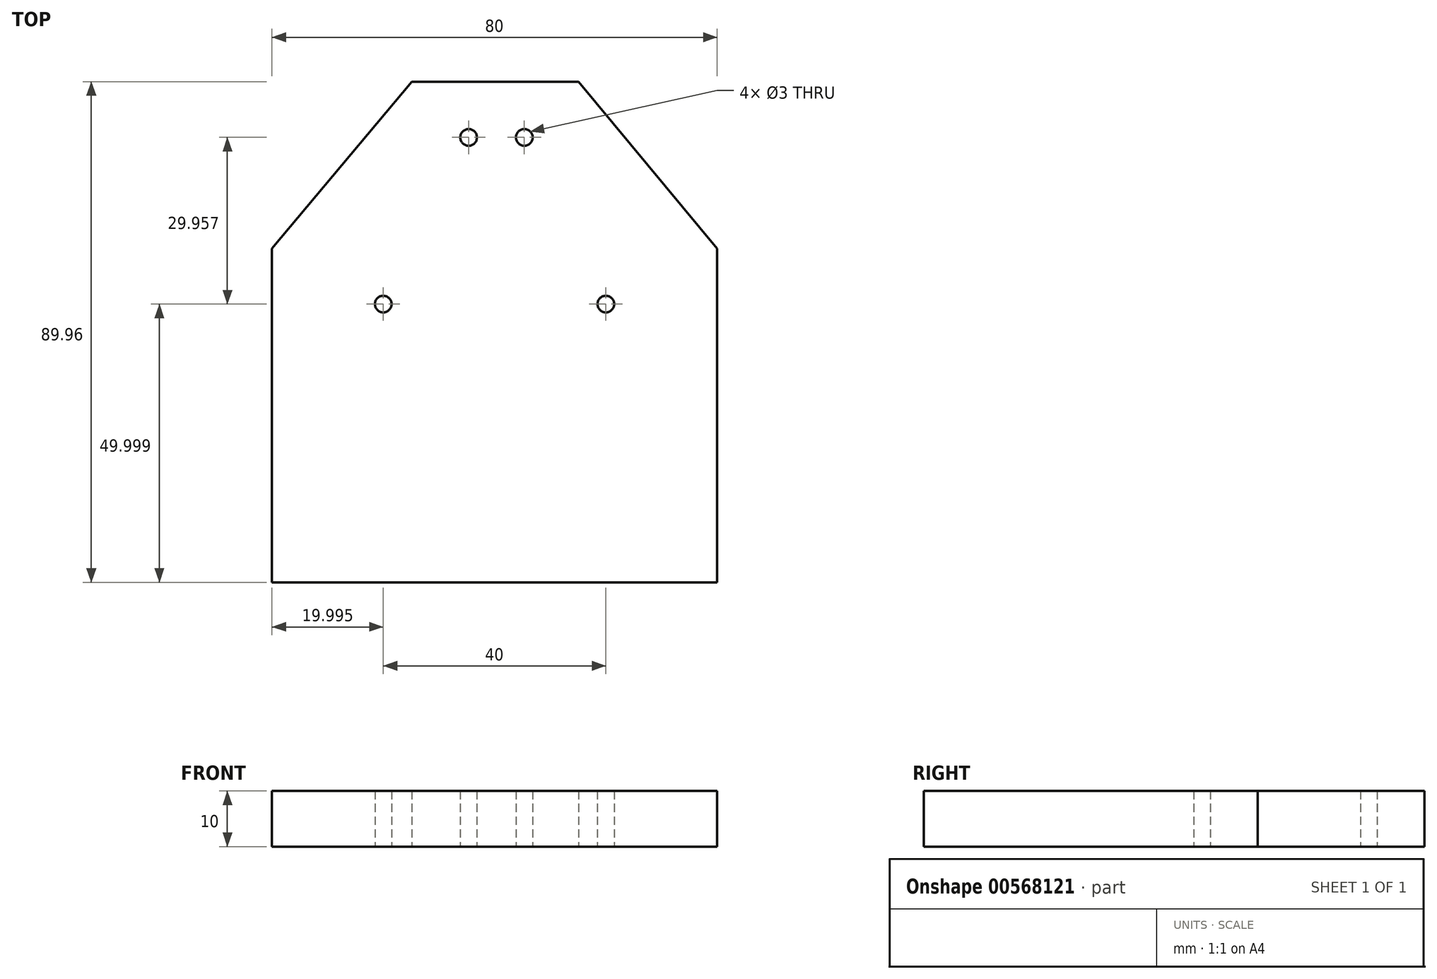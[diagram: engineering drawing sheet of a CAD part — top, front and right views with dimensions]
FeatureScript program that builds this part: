
annotation { "Feature Type Name" : "Feature", "Feature Type Description" : "" }
export const myFeature = defineFeature(function(context is Context, id is Id, definition is map)
    precondition{}
    {
        {
            var Q0;
            Q0=qCreatedBy(makeId("Top.planeOp"),FACE);
            var sketch = newSketch(context, id + "F0", { "sketchPlane" : qUnion([Q0])});
            skLineSegment(sketch, "E0", {"start": v(-40.34, 6.79) * mm, "end": v(39.66, 6.79) * mm});
            skLineSegment(sketch, "E1", {"start": v(39.66, 6.79) * mm, "end": v(39.66, 66.79) * mm});
            skLineSegment(sketch, "E2", {"start": v(-40.34, 6.79) * mm, "end": v(-40.34, 66.79) * mm});
            skLineSegment(sketch, "E3", {"start": v(-15.22, 96.75) * mm, "end": v(14.78, 96.75) * mm});
            skLineSegment(sketch, "E4", {"start": v(0, 66.79) * mm, "end": v(0, 96.79) * mm, "construction": true});
            skLineSegment(sketch, "E5", {"start": v(-15.22, 96.75) * mm, "end": v(-40.34, 66.79) * mm});
            skLineSegment(sketch, "E6", {"start": v(14.78, 96.75) * mm, "end": v(39.66, 66.79) * mm});
            skCircle(sketch, "E7", {"center": v(-20.34, 56.79) * mm, "radius": 1.5 * mm});
            skCircle(sketch, "E8", {"center": v(19.66, 56.79) * mm, "radius": 1.5 * mm});
            skCircle(sketch, "E9", {"center": v(5, 86.75) * mm, "radius": 1.5 * mm});
            skCircle(sketch, "E10", {"center": v(-5, 86.75) * mm, "radius": 1.5 * mm});
            skSolve(sketch);
        }
        {
            var Q0;
            Q0 = qSketchRegion(id + "F0", true);
            extrude(context, id + "F1", {"entities" : qUnion([Q0]), "depth" : 10 * mm, "offsetDistance" : 25 * mm});
        }
    });
